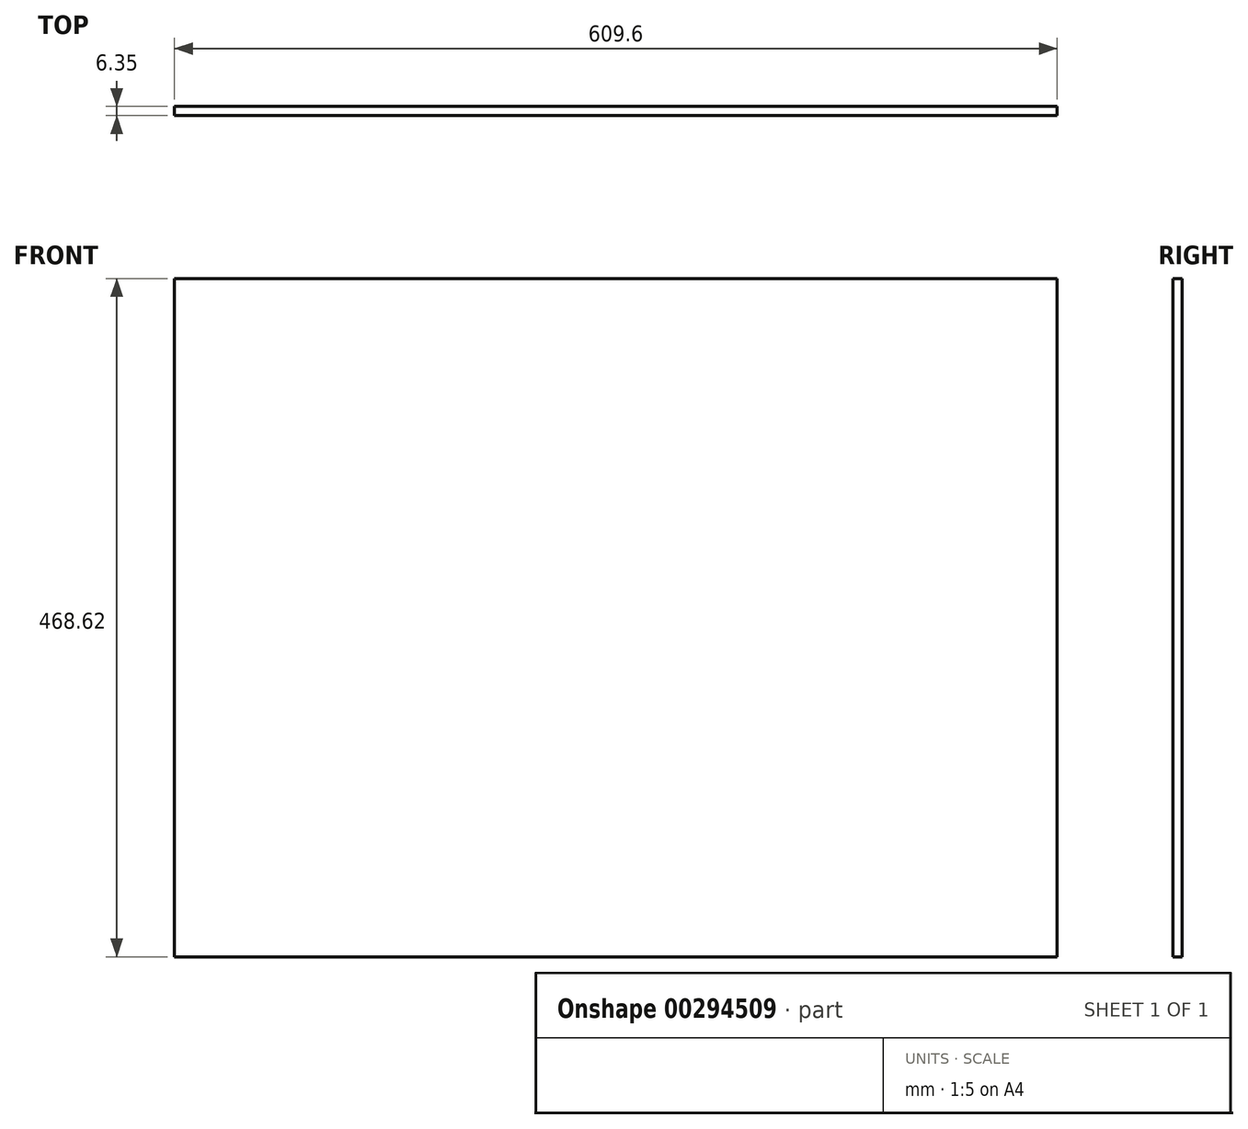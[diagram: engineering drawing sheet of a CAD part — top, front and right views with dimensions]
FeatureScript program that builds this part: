
annotation { "Feature Type Name" : "Feature", "Feature Type Description" : "" }
export const myFeature = defineFeature(function(context is Context, id is Id, definition is map)
    precondition{}
    {
        {
            var Q0;
            Q0=qCreatedBy(makeId("Front.planeOp"),FACE);
            var sketch = newSketch(context, id + "F0", { "sketchPlane" : qUnion([Q0])});
            skLineSegment(sketch, "E0.bottom", {"start": v(304.8, 234.32) * mm, "end": v(-304.8, 234.32) * mm});
            skLineSegment(sketch, "E0.top", {"start": v(304.8, -234.32) * mm, "end": v(-304.8, -234.32) * mm});
            skLineSegment(sketch, "E0.left", {"start": v(304.8, 234.32) * mm, "end": v(304.8, -234.31) * mm});
            skLineSegment(sketch, "E0.right", {"start": v(-304.8, 234.32) * mm, "end": v(-304.8, -234.31) * mm});
            skPoint(sketch, "E0.middle", {"position": v(0, 0) * mm});
            skSolve(sketch);
        }
        {
            var Q0;
            Q0=makeQuery(id+"F0.imprint","IMPRINT",FACE,{"disambiguationData":[TD([[makeQuery(id+"F0.imprint","IMPRINT",EDGE,{"derivedFrom":sQuery(id+"F0.wireOp",EDGE,"E0.bottom")}),1.0]])]});
            extrude(context, id + "F1", {"entities" : qUnion([Q0]), "depth" : 6.35 * mm});
        }
    });
